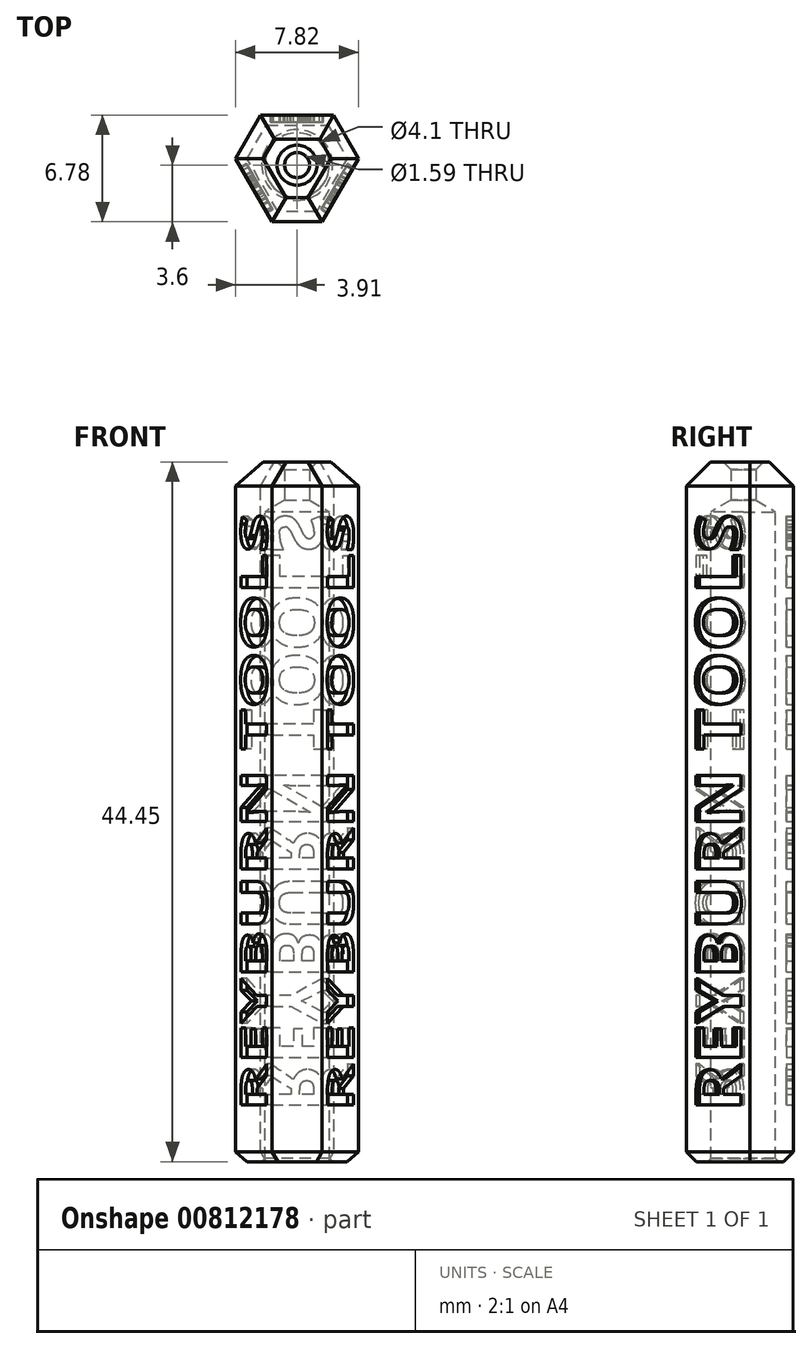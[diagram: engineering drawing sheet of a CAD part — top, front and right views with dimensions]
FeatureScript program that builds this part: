
annotation { "Feature Type Name" : "Feature", "Feature Type Description" : "" }
export const myFeature = defineFeature(function(context is Context, id is Id, definition is map)
    precondition{}
    {
        {
            var Q0;
            Q0=qCreatedBy(makeId("Top.planeOp"),FACE);
            var sketch = newSketch(context, id + "F0", { "sketchPlane" : qUnion([Q0])});
            skCircle(sketch, "E0.cCircle", {"center": v(0, 0) * mm, "radius": 6.35 * mm, "construction": true});
            skLineSegment(sketch, "E0.0", {"start": v(0, -6.35) * mm, "end": v(-5.5, 3.17) * mm});
            skLineSegment(sketch, "E0.1", {"start": v(-5.5, 3.18) * mm, "end": v(5.5, 3.18) * mm});
            skLineSegment(sketch, "E0.2", {"start": v(5.5, 3.18) * mm, "end": v(0, -6.35) * mm});
            skSolve(sketch);
        }
        {
            var Q0;
            Q0=makeQuery(id+"F0.imprint","IMPRINT",FACE,{"disambiguationData":[TD([[makeQuery(id+"F0.imprint","IMPRINT",EDGE,{"derivedFrom":sQuery(id+"F0.wireOp",EDGE,"E0.0")}),-1.0]])]});
            extrude(context, id + "F1", {"entities" : qUnion([Q0]), "oppositeDirection" : true, "depth" : 44.45 * mm, "offsetDistance" : 25.4 * mm});
        }
        {
            var Q0;
            Q0=makeQuery(id+"F1.opExtrude","CAP_FACE",FACE,{"disambiguationData":[OSD([sQuery(id+"F0.wireOp",EDGE,"E0.0"),sQuery(id+"F0.wireOp",EDGE,"E0.1"),sQuery(id+"F0.wireOp",EDGE,"E0.2")])],"isStart":false});
            var sketch = newSketch(context, id + "F2", { "sketchPlane" : qUnion([Q0])});
            skPoint(sketch, "E1", {"position": v(0, 0) * mm});
            skSolve(sketch);
        }
        {
            var Q0;
            Q0=sQuery(id+"F2.wireOp",VERTEX,"E1");
            var Q1;
            Q1=makeQuery(id+"F1.opExtrude","SWEPT_BODY",BODY,{"disambiguationData":[OSD([sQuery(id+"F0.wireOp",EDGE,"ghmTZ7Fa-hntI-yseL-cm0A-BedO1wdsdYtG")])]});
            var Q2;
            Q2=makeQuery(id+"F1.opExtrude","SWEPT_BODY",BODY,{"disambiguationData":[OSD([sQuery(id+"F0.wireOp",EDGE,"E0.0"),sQuery(id+"F0.wireOp",EDGE,"E0.1"),sQuery(id+"F0.wireOp",EDGE,"E0.2")])]});
            hole(context, id + "F3", {"style" : HoleStyle.C_SINK, "endStyle" : HoleEndStyle.BLIND, "offsetDistance" : 5 * mm, "threadStandard" : ThreadStandard.UNSET, "ansiThreadClass" : lookupTablePath({ "class" : "2B" }), "isoThreadClass" : lookupTablePath({ "class" : "6H" }), "holeDiameter" : 4.1 * mm, "holeDiameterToleranceBoundSymmetrical" : 0.1 * mm, "holeDiameterToleranceBoundDeviationUpper" : 0.1 * mm, "holeDiameterToleranceBoundDeviationLower" : -0.1 * mm, "holeDiameterToleranceBoundLimitsUpper" : 0.1 * mm, "holeDiameterToleranceBoundLimitsLower" : -0.1 * mm, "cBoreDiameterToleranceType" : ToleranceType.NONE, "cBoreDiameterToleranceBoundSymmetrical" : 0.1 * mm, "cBoreDiameterToleranceBoundDeviationUpper" : 0.1 * mm, "cBoreDiameterToleranceBoundDeviationLower" : -0.1 * mm, "cBoreDiameterToleranceBoundLimitsUpper" : 0.1 * mm, "cBoreDiameterToleranceBoundLimitsLower" : -0.1 * mm, "cBoreDepthToleranceType" : ToleranceType.NONE, "cBoreDepthToleranceBoundSymmetrical" : 0.1 * mm, "cBoreDepthToleranceBoundDeviationUpper" : 0.1 * mm, "cBoreDepthToleranceBoundDeviationLower" : -0.1 * mm, "cBoreDepthToleranceBoundLimitsUpper" : 0.1 * mm, "cBoreDepthToleranceBoundLimitsLower" : -0.1 * mm, "cSinkDiameter" : 4.5 * mm, "cSinkDiameterToleranceType" : ToleranceType.NONE, "cSinkDiameterToleranceBoundSymmetrical" : 0.1 * mm, "cSinkDiameterToleranceBoundDeviationUpper" : 0.1 * mm, "cSinkDiameterToleranceBoundDeviationLower" : -0.1 * mm, "cSinkDiameterToleranceBoundLimitsUpper" : 0.1 * mm, "cSinkDiameterToleranceBoundLimitsLower" : -0.1 * mm, "cSinkAngle" : 90 * degree, "cSinkAngleToleranceType" : ToleranceType.NONE, "cSinkAngleToleranceBoundSymmetrical" : 1 * degree, "cSinkAngleToleranceBoundDeviationUpper" : 1 * degree, "cSinkAngleToleranceBoundDeviationLower" : -1 * degree, "cSinkAngleToleranceBoundLimitsUpper" : 1 * degree, "cSinkAngleToleranceBoundLimitsLower" : -1 * degree, "tapDrillDiameterToleranceType" : ToleranceType.NONE, "tapDrillDiameterToleranceBoundSymmetrical" : 0.1 * mm, "tapDrillDiameterToleranceBoundDeviationUpper" : 0.1 * mm, "tapDrillDiameterToleranceBoundDeviationLower" : -0.1 * mm, "tapDrillDiameterToleranceBoundLimitsUpper" : 0.1 * mm, "tapDrillDiameterToleranceBoundLimitsLower" : -0.1 * mm, "majorDiameter" : 6.35 * mm, "holeDepthMultiple" : "Multiple", "holeDepthMultipleToleranceType" : ToleranceType.NONE, "holeDepthMultipleToleranceBoundSymmetrical" : 0.1 * mm, "holeDepthMultipleToleranceBoundDeviationUpper" : 0.1 * mm, "holeDepthMultipleToleranceBoundDeviationLower" : -0.1 * mm, "holeDepthMultipleToleranceBoundLimitsUpper" : 0.1 * mm, "holeDepthMultipleToleranceBoundLimitsLower" : -0.1 * mm, "holeDepthComputed" : 12 * mm, "holeDepthComputedToleranceType" : ToleranceType.NONE, "holeDepthComputedToleranceBoundSymmetrical" : 0.1 * mm, "holeDepthComputedToleranceBoundDeviationUpper" : 0.1 * mm, "holeDepthComputedToleranceBoundDeviationLower" : -0.1 * mm, "holeDepthComputedToleranceBoundLimitsUpper" : 0.1 * mm, "holeDepthComputedToleranceBoundLimitsLower" : -0.1 * mm, "holeDepth" : 41.27 * mm, "holeDepthToleranceType" : ToleranceType.NONE, "holeDepthToleranceBoundSymmetrical" : 0.1 * mm, "holeDepthToleranceBoundDeviationUpper" : 0.1 * mm, "holeDepthToleranceBoundDeviationLower" : -0.1 * mm, "holeDepthToleranceBoundLimitsUpper" : 0.1 * mm, "holeDepthToleranceBoundLimitsLower" : -0.1 * mm, "tipAngleStyle" : TipAngleStyle.DEGREE118, "tipAngle" : 118 * degree, "tipAngleToleranceType" : ToleranceType.NONE, "tipAngleToleranceBoundSymmetrical" : 1 * degree, "tipAngleToleranceBoundDeviationUpper" : 1 * degree, "tipAngleToleranceBoundDeviationLower" : -1 * degree, "tipAngleToleranceBoundLimitsUpper" : 1 * degree, "tipAngleToleranceBoundLimitsLower" : -1 * degree, "isTappedThrough" : true, "tappedDepth" : 12.7 * mm, "tappedDepthToleranceType" : ToleranceType.NONE, "tappedDepthToleranceBoundSymmetrical" : 0.1 * mm, "tappedDepthToleranceBoundDeviationUpper" : 0.1 * mm, "tappedDepthToleranceBoundDeviationLower" : -0.1 * mm, "tappedDepthToleranceBoundLimitsUpper" : 0.1 * mm, "tappedDepthToleranceBoundLimitsLower" : -0.1 * mm, "tappedAngle" : 1.79 * degree, "tapClearance" : 3, "locations" : qUnion([Q0]), "scope" : qUnion([Q1, Q2]), "startStyle" : HoleStartStyle.PART, "holeDiameterToleranceType" : ToleranceTypeExtended.NONE});
        }
        {
            var Q0;
            Q0=makeQuery(id+"F1.opExtrude","SWEPT_EDGE",EDGE,{"disambiguationData":[OSD([sQuery(id+"F0.wireOp",EDGE,"E0.0"),sQuery(id+"F0.wireOp",EDGE,"E0.2")])]});
            var Q1;
            Q1=makeQuery(id+"F1.opExtrude","SWEPT_EDGE",EDGE,{"disambiguationData":[OSD([sQuery(id+"F0.wireOp",EDGE,"E0.1"),sQuery(id+"F0.wireOp",EDGE,"E0.2")])]});
            var Q2;
            Q2=makeQuery(id+"F1.opExtrude","SWEPT_EDGE",EDGE,{"disambiguationData":[OSD([sQuery(id+"F0.wireOp",EDGE,"E0.0"),sQuery(id+"F0.wireOp",EDGE,"E0.1")])]});
            chamfer(context, id + "F4", {"entities" : qUnion([Q0, Q1, Q2]), "width" : 3.17 * mm, "tangentPropagation" : true});
        }
        {
            var Q0;
            Q0=makeQuery(id+"F1.opExtrude","SWEPT_FACE",FACE,{"disambiguationData":[OSD([sQuery(id+"F0.wireOp",EDGE,"E0.1")])]});
            var sketch = newSketch(context, id + "F5", { "sketchPlane" : qUnion([Q0])});
            skText(sketch, "E2", { "text": "REYBURN TOOLS", "fontName": "OpenSans-Bold.ttf"});
            skLineSegment(sketch, "E3", {"start": v(0, 0) * mm, "end": v(0, -3.18) * mm, "construction": true});
            const initialGuessF5  = {"E2": [0.00165, -0.04127, 0, 1, 0.0033]};
            skSetInitialGuess(sketch, initialGuessF5);
            skSolve(sketch);
        }
        {
            var Q0;
            Q0 = qSketchRegion(id + "F5", true);
            var Q1;
            Q1 = qSketchRegion(id + "F7", true);
            extrude(context, id + "F6", {"entities" : qUnion([Q0, Q1]), "operationType" : NewBodyOperationType.REMOVE, "oppositeDirection" : true, "depth" : 0.43 * mm, "offsetDistance" : 25.4 * mm});
        }
        {
            var Q0;
            Q0=makeQuery(id+"F1.opExtrude","SWEPT_FACE",FACE,{"disambiguationData":[OSD([sQuery(id+"F0.wireOp",EDGE,"E0.0")])]});
            var sketch = newSketch(context, id + "F7", { "sketchPlane" : qUnion([Q0])});
            skText(sketch, "E4", { "text": "REYBURN TOOLS", "fontName": "OpenSans-Bold.ttf"});
            skLineSegment(sketch, "E5", {"start": v(0, 0) * mm, "end": v(0, -3.18) * mm, "construction": true});
            const initialGuessF7  = {"E4": [0.00165, -0.04127, 0, 1, 0.0033]};
            skSetInitialGuess(sketch, initialGuessF7);
            skSolve(sketch);
        }
        {
            var Q0;
            Q0 = qSketchRegion(id + "F7", true);
            extrude(context, id + "F8", {"entities" : qUnion([Q0]), "operationType" : NewBodyOperationType.REMOVE, "oppositeDirection" : true, "depth" : 0.43 * mm, "offsetDistance" : 25.4 * mm});
        }
        {
            var Q0;
            Q0=makeQuery(id+"F1.opExtrude","SWEPT_FACE",FACE,{"disambiguationData":[OSD([sQuery(id+"F0.wireOp",EDGE,"E0.2")])]});
            var sketch = newSketch(context, id + "F9", { "sketchPlane" : qUnion([Q0])});
            skText(sketch, "E6", { "text": "REYBURN TOOLS", "fontName": "OpenSans-Bold.ttf"});
            skLineSegment(sketch, "E7", {"start": v(0, 0) * mm, "end": v(0, -3.18) * mm, "construction": true});
            const initialGuessF9  = {"E6": [0.00165, -0.04127, 0, 1, 0.0033]};
            skSetInitialGuess(sketch, initialGuessF9);
            skSolve(sketch);
        }
        {
            var Q0;
            Q0 = qSketchRegion(id + "F9", true);
            extrude(context, id + "F10", {"entities" : qUnion([Q0]), "operationType" : NewBodyOperationType.REMOVE, "oppositeDirection" : true, "depth" : 0.43 * mm, "offsetDistance" : 25.4 * mm});
        }
        {
            var Q0;
            Q0=makeQuery(id+"F1.opExtrude","CAP_FACE",FACE,{"disambiguationData":[OSD([sQuery(id+"F0.wireOp",EDGE,"E0.0"),sQuery(id+"F0.wireOp",EDGE,"E0.1"),sQuery(id+"F0.wireOp",EDGE,"E0.2")])],"isStart":true});
            var sketch = newSketch(context, id + "F11", { "sketchPlane" : qUnion([Q0])});
            skPoint(sketch, "E8", {"position": v(0, 0) * mm});
            skSolve(sketch);
        }
        {
            var Q0;
            Q0=sQuery(id+"F11.wireOp",VERTEX,"E8");
            var Q1;
            Q1=makeQuery(id+"F1.opExtrude","SWEPT_BODY",BODY,{"disambiguationData":[OSD([sQuery(id+"F0.wireOp",EDGE,"E0.0"),sQuery(id+"F0.wireOp",EDGE,"E0.1"),sQuery(id+"F0.wireOp",EDGE,"E0.2")])]});
            hole(context, id + "F12", {"style" : HoleStyle.C_SINK, "endStyle" : HoleEndStyle.THROUGH, "holeDiameter" : 1.59 * mm, "cSinkDiameter" : 2.54 * mm, "cSinkAngle" : 90 * degree, "majorDiameter" : 6.35 * mm, "isTappedThrough" : true, "tappedDepth" : 12.7 * mm, "tapClearance" : 3, "locations" : qUnion([Q0]), "scope" : qUnion([Q1]), "startStyle" : HoleStartStyle.PART});
        }
        {
            var Q0;
            Q0=makeQuery(id+"F1.opExtrude","CAP_EDGE",EDGE,{"disambiguationData":[OSD([sQuery(id+"F0.wireOp",EDGE,"E0.0")])],"isStart":false});
            var Q1;
            {var subQ0=sQuery(id+"F0.wireOp",EDGE,"E0.1");var subQ1=sQuery(id+"F0.wireOp",EDGE,"E0.0");Q1=makeQuery(id+"F4.opChamfer","BLEND_EDGE",EDGE,{"blendedFrom":[makeQuery(id+"F1.opExtrude","SWEPT_EDGE",EDGE,{"disambiguationData":[OSD([subQ1,subQ0])]}),makeQuery(id+"F1.opExtrude","CAP_FACE",FACE,{"disambiguationData":[OSD([subQ1,subQ0,sQuery(id+"F0.wireOp",EDGE,"E0.2")])],"isStart":false})],"blendedInto":[makeQuery(id+"F1.opExtrude","CAP_FACE",FACE,{"disambiguationData":[OSD([subQ1,subQ0,sQuery(id+"F0.wireOp",EDGE,"E0.2")])],"isStart":false})]});}
            var Q2;
            Q2=makeQuery(id+"F1.opExtrude","CAP_EDGE",EDGE,{"disambiguationData":[OSD([sQuery(id+"F0.wireOp",EDGE,"E0.1")])],"isStart":false});
            var Q3;
            {var subQ0=sQuery(id+"F0.wireOp",EDGE,"E0.2");var subQ1=sQuery(id+"F0.wireOp",EDGE,"E0.1");Q3=makeQuery(id+"F4.opChamfer","BLEND_EDGE",EDGE,{"blendedFrom":[makeQuery(id+"F1.opExtrude","SWEPT_EDGE",EDGE,{"disambiguationData":[OSD([subQ1,subQ0])]}),makeQuery(id+"F1.opExtrude","CAP_FACE",FACE,{"disambiguationData":[OSD([sQuery(id+"F0.wireOp",EDGE,"E0.0"),subQ1,subQ0])],"isStart":false})],"blendedInto":[makeQuery(id+"F1.opExtrude","CAP_FACE",FACE,{"disambiguationData":[OSD([sQuery(id+"F0.wireOp",EDGE,"E0.0"),subQ1,subQ0])],"isStart":false})]});}
            var Q4;
            Q4=makeQuery(id+"F1.opExtrude","CAP_EDGE",EDGE,{"disambiguationData":[OSD([sQuery(id+"F0.wireOp",EDGE,"E0.2")])],"isStart":false});
            var Q5;
            {var subQ0=sQuery(id+"F0.wireOp",EDGE,"E0.2");var subQ1=sQuery(id+"F0.wireOp",EDGE,"E0.0");Q5=makeQuery(id+"F4.opChamfer","BLEND_EDGE",EDGE,{"blendedFrom":[makeQuery(id+"F1.opExtrude","SWEPT_EDGE",EDGE,{"disambiguationData":[OSD([subQ1,subQ0])]}),makeQuery(id+"F1.opExtrude","CAP_FACE",FACE,{"disambiguationData":[OSD([subQ1,sQuery(id+"F0.wireOp",EDGE,"E0.1"),subQ0])],"isStart":false})],"blendedInto":[makeQuery(id+"F1.opExtrude","CAP_FACE",FACE,{"disambiguationData":[OSD([subQ1,sQuery(id+"F0.wireOp",EDGE,"E0.1"),subQ0])],"isStart":false})]});}
            chamfer(context, id + "F13", {"entities" : qUnion([Q0, Q1, Q2, Q3, Q4, Q5]), "width" : 0.64 * mm, "tangentPropagation" : true});
        }
        {
            var Q0;
            Q0=makeQuery(id+"F1.opExtrude","CAP_EDGE",EDGE,{"disambiguationData":[OSD([sQuery(id+"F0.wireOp",EDGE,"E0.2")])],"isStart":true});
            var Q1;
            {var subQ0=sQuery(id+"F0.wireOp",EDGE,"E0.2");var subQ1=sQuery(id+"F0.wireOp",EDGE,"E0.0");Q1=makeQuery(id+"F4.opChamfer","BLEND_EDGE",EDGE,{"blendedFrom":[makeQuery(id+"F1.opExtrude","SWEPT_EDGE",EDGE,{"disambiguationData":[OSD([subQ1,subQ0])]}),makeQuery(id+"F1.opExtrude","CAP_FACE",FACE,{"disambiguationData":[OSD([subQ1,sQuery(id+"F0.wireOp",EDGE,"E0.1"),subQ0])],"isStart":true})],"blendedInto":[makeQuery(id+"F1.opExtrude","CAP_FACE",FACE,{"disambiguationData":[OSD([subQ1,sQuery(id+"F0.wireOp",EDGE,"E0.1"),subQ0])],"isStart":true})]});}
            var Q2;
            Q2=makeQuery(id+"F1.opExtrude","CAP_EDGE",EDGE,{"disambiguationData":[OSD([sQuery(id+"F0.wireOp",EDGE,"E0.0")])],"isStart":true});
            var Q3;
            {var subQ0=sQuery(id+"F0.wireOp",EDGE,"E0.1");var subQ1=sQuery(id+"F0.wireOp",EDGE,"E0.0");Q3=makeQuery(id+"F4.opChamfer","BLEND_EDGE",EDGE,{"blendedFrom":[makeQuery(id+"F1.opExtrude","SWEPT_EDGE",EDGE,{"disambiguationData":[OSD([subQ1,subQ0])]}),makeQuery(id+"F1.opExtrude","CAP_FACE",FACE,{"disambiguationData":[OSD([subQ1,subQ0,sQuery(id+"F0.wireOp",EDGE,"E0.2")])],"isStart":true})],"blendedInto":[makeQuery(id+"F1.opExtrude","CAP_FACE",FACE,{"disambiguationData":[OSD([subQ1,subQ0,sQuery(id+"F0.wireOp",EDGE,"E0.2")])],"isStart":true})]});}
            var Q4;
            Q4=makeQuery(id+"F1.opExtrude","CAP_EDGE",EDGE,{"disambiguationData":[OSD([sQuery(id+"F0.wireOp",EDGE,"E0.1")])],"isStart":true});
            var Q5;
            {var subQ0=sQuery(id+"F0.wireOp",EDGE,"E0.2");var subQ1=sQuery(id+"F0.wireOp",EDGE,"E0.1");Q5=makeQuery(id+"F4.opChamfer","BLEND_EDGE",EDGE,{"blendedFrom":[makeQuery(id+"F1.opExtrude","SWEPT_EDGE",EDGE,{"disambiguationData":[OSD([subQ1,subQ0])]}),makeQuery(id+"F1.opExtrude","CAP_FACE",FACE,{"disambiguationData":[OSD([sQuery(id+"F0.wireOp",EDGE,"E0.0"),subQ1,subQ0])],"isStart":true})],"blendedInto":[makeQuery(id+"F1.opExtrude","CAP_FACE",FACE,{"disambiguationData":[OSD([sQuery(id+"F0.wireOp",EDGE,"E0.0"),subQ1,subQ0])],"isStart":true})]});}
            chamfer(context, id + "F14", {"entities" : qUnion([Q0, Q1, Q2, Q3, Q4, Q5]), "width" : 1.52 * mm, "tangentPropagation" : true});
        }
    });
